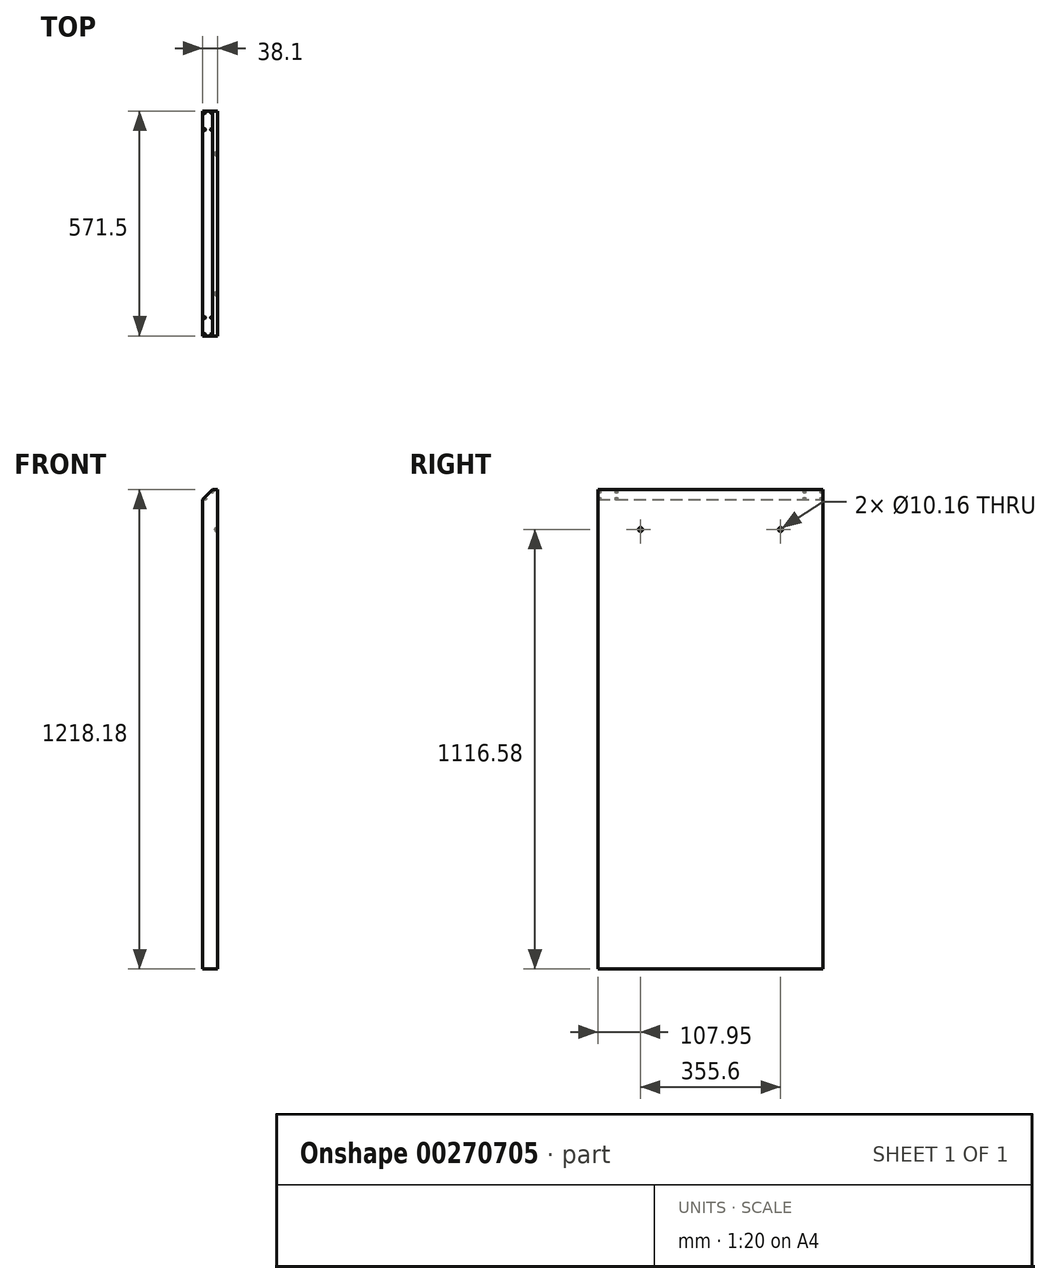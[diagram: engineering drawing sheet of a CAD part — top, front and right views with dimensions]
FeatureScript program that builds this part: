
annotation { "Feature Type Name" : "Feature", "Feature Type Description" : "" }
export const myFeature = defineFeature(function(context is Context, id is Id, definition is map)
    precondition{}
    {
        {
            var Q0;
            Q0=qCreatedBy(makeId("Front.planeOp"),FACE);
            var sketch = newSketch(context, id + "F0", { "sketchPlane" : qUnion([Q0])});
            skLineSegment(sketch, "E0.bottom", {"start": v(0, 0) * mm, "end": v(38.1, 0) * mm});
            skLineSegment(sketch, "E0.top", {"start": v(0, 1218.18) * mm, "end": v(38.1, 1218.18) * mm});
            skLineSegment(sketch, "E0.left", {"start": v(0, 0) * mm, "end": v(0, 1218.18) * mm});
            skLineSegment(sketch, "E0.right", {"start": v(38.1, 0) * mm, "end": v(38.1, 1218.18) * mm});
            skSolve(sketch);
        }
        {
            var Q0;
            Q0 = qSketchRegion(id + "F0", true);
            extrude(context, id + "F1", {"entities" : qUnion([Q0]), "depth" : 571.5 * mm});
        }
        {
            var Q0;
            Q0=makeQuery(id+"F1.opExtrude","SWEPT_EDGE",EDGE,{"disambiguationData":[OSD([sQuery(id+"F0.wireOp",EDGE,"E0.top"),sQuery(id+"F0.wireOp",EDGE,"E0.left")])]});
            chamfer(context, id + "F2", {"entities" : qUnion([Q0]), "chamferType" : ChamferType.OFFSET_ANGLE, "width" : 25.4 * mm, "oppositeDirection" : false, "angle" : 45 * degree, "tangentPropagation" : true});
        }
        {
            var Q0;
            Q0=makeQuery(id+"F2.opChamfer","BLEND_FACE",FACE,{"disambiguationData":[OSD([sQuery(id+"F0.wireOp",EDGE,"E0.top"),sQuery(id+"F0.wireOp",EDGE,"E0.left")])]});
            var sketch = newSketch(context, id + "F3", { "sketchPlane" : qUnion([Q0])});
            skPoint(sketch, "E1.endSnap0", {"position": v(25.4, 861.39) * mm});
            skPoint(sketch, "E2", {"position": v(3.96, 874.09) * mm});
            skPoint(sketch, "E3", {"position": v(3.96, 848.69) * mm});
            skPoint(sketch, "E4.MirrorP", {"position": v(46.84, 874.09) * mm});
            skPoint(sketch, "E5.MirrorP", {"position": v(46.84, 848.69) * mm});
            skLineSegment(sketch, "E6", {"start": v(285.75, 879.35) * mm, "end": v(285.75, 843.43) * mm});
            skPoint(sketch, "E7.MirrorP", {"position": v(567.54, 874.09) * mm});
            skPoint(sketch, "E8.MirrorP", {"position": v(567.54, 848.69) * mm});
            skPoint(sketch, "E9.MirrorP", {"position": v(524.66, 848.69) * mm});
            skPoint(sketch, "E10.MirrorP", {"position": v(524.66, 874.09) * mm});
            skSolve(sketch);
        }
        {
            var Q0;
            Q0=sQuery(id+"F3.wireOp",VERTEX,"E2");
            var Q1;
            Q1=sQuery(id+"F3.wireOp",VERTEX,"E3");
            var Q2;
            Q2=sQuery(id+"F3.wireOp",VERTEX,"E4.MirrorP");
            var Q3;
            Q3=sQuery(id+"F3.wireOp",VERTEX,"E5.MirrorP");
            var Q4;
            Q4=sQuery(id+"F3.wireOp",VERTEX,"E10.MirrorP");
            var Q5;
            Q5=sQuery(id+"F3.wireOp",VERTEX,"E9.MirrorP");
            var Q6;
            Q6=sQuery(id+"F3.wireOp",VERTEX,"E8.MirrorP");
            var Q7;
            Q7=sQuery(id+"F3.wireOp",VERTEX,"E7.MirrorP");
            var Q8;
            Q8=makeQuery(id+"F1.opExtrude","SWEPT_BODY",BODY,{"disambiguationData":[OSD([sQuery(id+"F0.wireOp",EDGE,"E0.bottom"),sQuery(id+"F0.wireOp",EDGE,"E0.top"),sQuery(id+"F0.wireOp",EDGE,"E0.left"),sQuery(id+"F0.wireOp",EDGE,"E0.right")])]});
            hole(context, id + "F4", {"style" : HoleStyle.SIMPLE, "endStyle" : HoleEndStyle.BLIND, "holeDiameter" : 5.08 * mm, "holeDepth" : 5.08 * mm, "tappedDepth" : 12.7 * mm, "tapClearance" : 3, "locations" : qUnion([Q0, Q1, Q2, Q3, Q4, Q5, Q6, Q7]), "scope" : qUnion([Q8])});
        }
        {
            var Q0;
            Q0=makeQuery(id+"F1.opExtrude","SWEPT_FACE",FACE,{"disambiguationData":[OSD([sQuery(id+"F0.wireOp",EDGE,"E0.right")])]});
            var sketch = newSketch(context, id + "F5", { "sketchPlane" : qUnion([Q0])});
            skPoint(sketch, "E11", {"position": v(-463.55, 1116.58) * mm});
            skPoint(sketch, "E12", {"position": v(-107.95, 1116.58) * mm});
            skSolve(sketch);
        }
        {
            var Q0;
            Q0=sQuery(id+"F5.wireOp",VERTEX,"E11");
            var Q1;
            Q1=sQuery(id+"F5.wireOp",VERTEX,"E12");
            var Q2;
            Q2=makeQuery(id+"F1.opExtrude","SWEPT_BODY",BODY,{"disambiguationData":[OSD([sQuery(id+"F0.wireOp",EDGE,"E0.bottom"),sQuery(id+"F0.wireOp",EDGE,"E0.top"),sQuery(id+"F0.wireOp",EDGE,"E0.left"),sQuery(id+"F0.wireOp",EDGE,"E0.right")])]});
            hole(context, id + "F6", {"style" : HoleStyle.SIMPLE, "endStyle" : HoleEndStyle.BLIND, "holeDiameter" : 10.16 * mm, "holeDepth" : 5.08 * mm, "tappedDepth" : 12.7 * mm, "tapClearance" : 3, "locations" : qUnion([Q0, Q1]), "scope" : qUnion([Q2])});
        }
    });
